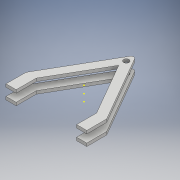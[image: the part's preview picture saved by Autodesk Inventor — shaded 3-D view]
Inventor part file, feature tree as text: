
AUTODESK INVENTOR PART (.ipt)
format: ipt  version: 2018 (Build 220112000, 112)  size: 167,424 bytes
history: native  units: mm
features: sketch x9, extrude x5, plane x3, mirror x3, fillet x1
ambient origin geometry x8: Origin, YZ Plane, XZ Plane, XY Plane, X Axis, Y Axis, Z Axis, Center Point
bodies: Body1 (feature_tree)
feature tree (21):
  extrude  "Extrusion5"  Depth=17.5mm TaperAngle=0.0deg
  sketch  "Sketch6"  dims[d15=50.0mm d16=323.25mm d17=0.0mm]
  sketch  "Sketch7"  dims[d18=130.25mm d19=0.0mm d20=22.5mm d21=15.0mm]
  extrude  "Extrusion6"  Depth=50.0mm TaperAngle=0.0deg
  extrude  "Extrusion7"  Depth=15.0mm
  plane  "Work Plane2"
  sketch  "Sketch10"
  mirror  "Mirror3"
  fillet  "Fillet3"  Radius=15.0mm
  extrude  "Extrusion8"  Depth=114.8mm
  extrude  "Extrusion9"  [1 undecoded]
  sketch  "Sketch13"
  plane  "Work Plane3"
  mirror  "Mirror4"
  mirror  "Mirror5"
  sketch  "Sketch5"  dims[d12=519.6mm d13=17.5mm d14=0.0mm]
  sketch  "Sketch8"  dims[d22=474.75mm d23=0.0mm d24=114.8mm]
  sketch  "Sketch9"  dims[d25=17.5mm d26=0.0mm]
  sketch  "Sketch11"
  sketch  "Sketch12"
  plane  "Work Plane4"
note: 1 required parameter value undecoded (feature->parameter linkage not recoverable at this tier; creation-order binding heuristic only, values carry confidence <= 0.55)
